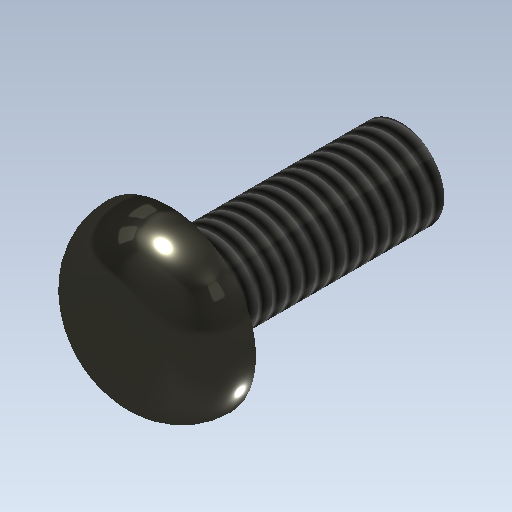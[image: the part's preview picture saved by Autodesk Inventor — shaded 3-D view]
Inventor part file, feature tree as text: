
AUTODESK INVENTOR PART (.ipt)
format: ipt  version: 2020.2 (Build 242310000, 310)  size: 179,200 bytes
history: native  units: mm
features: extrude x3, sketch x3, other x1, fillet x1, thread x1
ambient origin geometry x1: Origin
bodies: Body1 (feature_tree)
feature tree (9):
  other  "ソリッド1"
  extrude  "押し出し1"  Depth=3.0mm
  extrude  "押し出し2"  Depth=6.0mm TaperAngle=0.0deg
  fillet  "フィレット1"  Radius=6.0mm
  thread  "ねじ1"
  extrude  "押し出し3"  Depth=2.0mm TaperAngle=0.0deg
  sketch  "スケッチ1"
  sketch  "スケッチ2"
  sketch  "スケッチ3"
